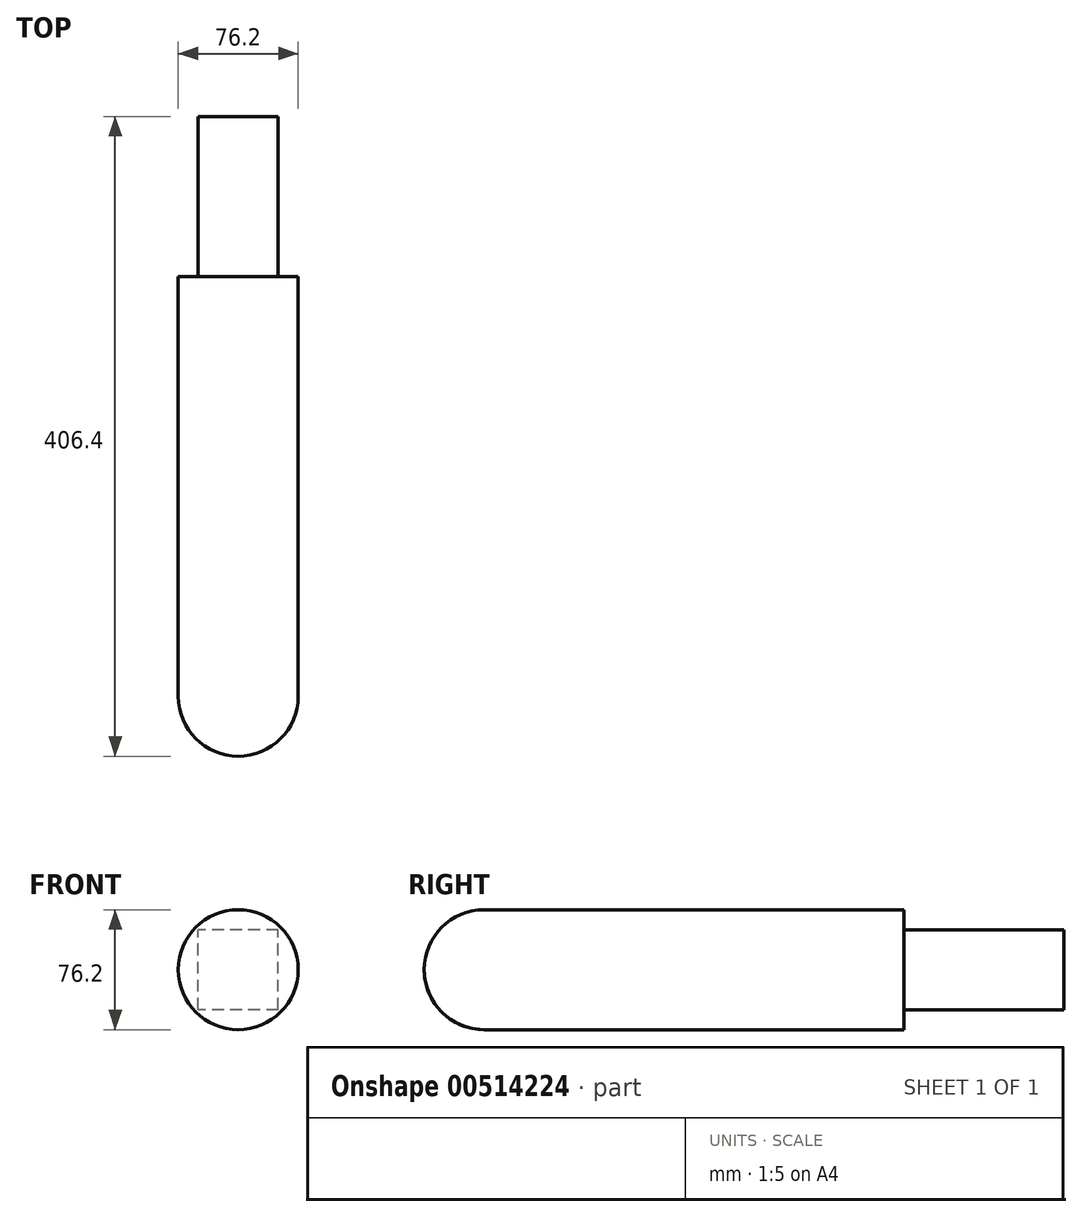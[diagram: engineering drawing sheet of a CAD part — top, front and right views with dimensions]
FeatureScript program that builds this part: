
annotation { "Feature Type Name" : "Feature", "Feature Type Description" : "" }
export const myFeature = defineFeature(function(context is Context, id is Id, definition is map)
    precondition{}
    {
        {
            var Q0;
            Q0=qCreatedBy(makeId("Front.planeOp"),FACE);
            var sketch = newSketch(context, id + "F0", { "sketchPlane" : qUnion([Q0])});
            skLineSegment(sketch, "E0.bottom", {"start": v(25.4, -25.4) * mm, "end": v(-25.4, -25.4) * mm});
            skLineSegment(sketch, "E0.top", {"start": v(25.4, 25.4) * mm, "end": v(-25.4, 25.4) * mm});
            skLineSegment(sketch, "E0.left", {"start": v(25.4, -25.4) * mm, "end": v(25.4, 25.4) * mm});
            skLineSegment(sketch, "E0.right", {"start": v(-25.4, -25.4) * mm, "end": v(-25.4, 25.4) * mm});
            skPoint(sketch, "E0.middle", {"position": v(0, 0) * mm});
            skSolve(sketch);
        }
        {
            var Q0;
            Q0 = qSketchRegion(id + "F0", true);
            extrude(context, id + "F1", {"entities" : qUnion([Q0]), "depth" : 101.6 * mm, "offsetDistance" : 25.4 * mm});
        }
        {
            var Q0;
            Q0=makeQuery(id+"F1.opExtrude","CAP_FACE",FACE,{"disambiguationData":[OSD([sQuery(id+"F0.wireOp",EDGE,"E0.bottom"),sQuery(id+"F0.wireOp",EDGE,"E0.top"),sQuery(id+"F0.wireOp",EDGE,"E0.left"),sQuery(id+"F0.wireOp",EDGE,"E0.right")])],"isStart":false});
            var sketch = newSketch(context, id + "F2", { "sketchPlane" : qUnion([Q0])});
            skCircle(sketch, "E1", {"center": v(0, 0) * mm, "radius": 38.1 * mm});
            skSolve(sketch);
        }
        {
            var Q0;
            Q0 = qSketchRegion(id + "F2", true);
            extrude(context, id + "F3", {"entities" : qUnion([Q0]), "operationType" : NewBodyOperationType.ADD, "depth" : 304.8 * mm, "offsetDistance" : 25.4 * mm});
        }
        {
            var Q0;
            Q0=makeQuery(id+"F3.opExtrude","CAP_FACE",FACE,{"disambiguationData":[OSD([sQuery(id+"F2.wireOp",EDGE,"E1")])],"isStart":false});
            fillet(context, id + "F4", {"entities" : qUnion([Q0]), "radius" : 38.1 * mm, "tangentPropagation" : true, "allowEdgeOverflow" : false});
        }
    });
